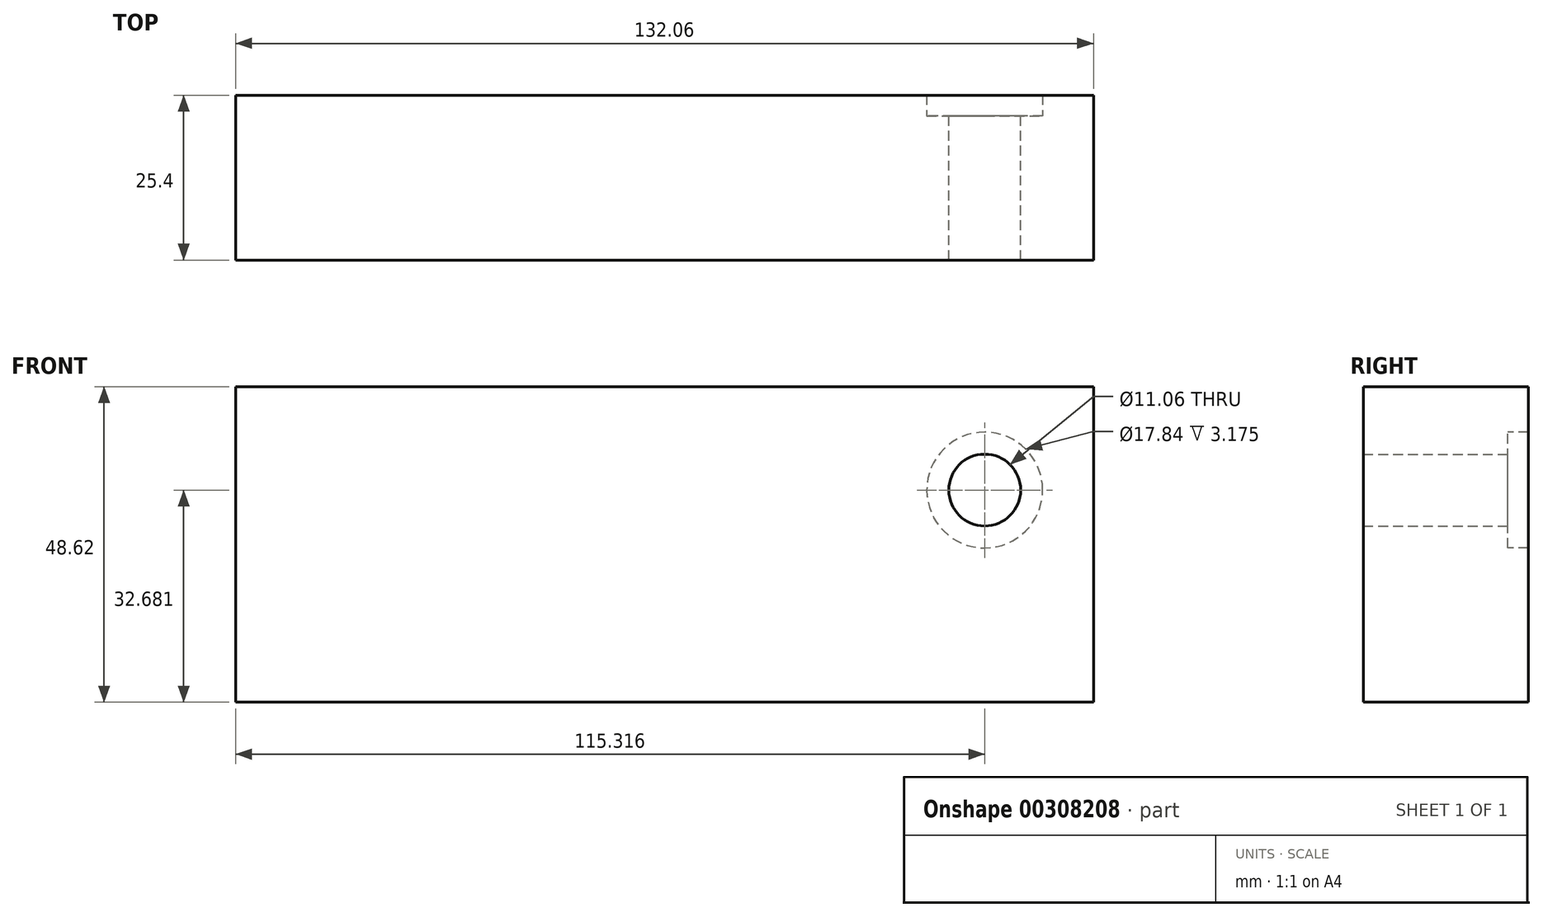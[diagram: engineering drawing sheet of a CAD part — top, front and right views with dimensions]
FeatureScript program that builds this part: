
annotation { "Feature Type Name" : "Feature", "Feature Type Description" : "" }
export const myFeature = defineFeature(function(context is Context, id is Id, definition is map)
    precondition{}
    {
        {
            var Q0;
            Q0=qCreatedBy(makeId("Front.planeOp"),FACE);
            var sketch = newSketch(context, id + "F0", { "sketchPlane" : qUnion([Q0])});
            skLineSegment(sketch, "E0.bottom", {"start": v(-66.03, 24.31) * mm, "end": v(66.03, 24.31) * mm});
            skLineSegment(sketch, "E0.top", {"start": v(-66.03, -24.31) * mm, "end": v(66.03, -24.31) * mm});
            skLineSegment(sketch, "E0.left", {"start": v(-66.03, 24.31) * mm, "end": v(-66.03, -24.31) * mm});
            skLineSegment(sketch, "E0.right", {"start": v(66.03, 24.31) * mm, "end": v(66.03, -24.31) * mm});
            skPoint(sketch, "E0.middle", {"position": v(0, 0) * mm});
            skCircle(sketch, "E1", {"center": v(49.29, 8.37) * mm, "radius": 5.53 * mm});
            skCircle(sketch, "E2", {"center": v(49.29, 8.37) * mm, "radius": 8.92 * mm});
            skSolve(sketch);
        }
        {
            var Q0;
            Q0=makeQuery(id+"F0.imprint","IMPRINT",FACE,{"disambiguationData":[TD([[makeQuery(id+"F0.imprint","IMPRINT",EDGE,{"derivedFrom":sQuery(id+"F0.wireOp",EDGE,"E0.bottom")}),-1.0]])]});
            var Q1;
            Q1=makeQuery(id+"F0.imprint","IMPRINT",FACE,{"disambiguationData":[TD([[makeQuery(id+"F0.imprint","IMPRINT",EDGE,{"derivedFrom":sQuery(id+"F0.wireOp",EDGE,"E1")}),-1.0]])]});
            extrude(context, id + "F1", {"entities" : qUnion([Q0, Q1]), "depth" : 25.4 * mm});
        }
        {
            var Q0;
            Q0=makeQuery(id+"F0.imprint","IMPRINT",FACE,{"disambiguationData":[TD([[makeQuery(id+"F0.imprint","IMPRINT",EDGE,{"derivedFrom":sQuery(id+"F0.wireOp",EDGE,"E1")}),-1.0]])]});
            extrude(context, id + "F2", {"entities" : qUnion([Q0]), "operationType" : NewBodyOperationType.REMOVE, "endBound" : BoundingType.SYMMETRIC, "oppositeDirection" : true, "depth" : 6.35 * mm});
        }
    });
